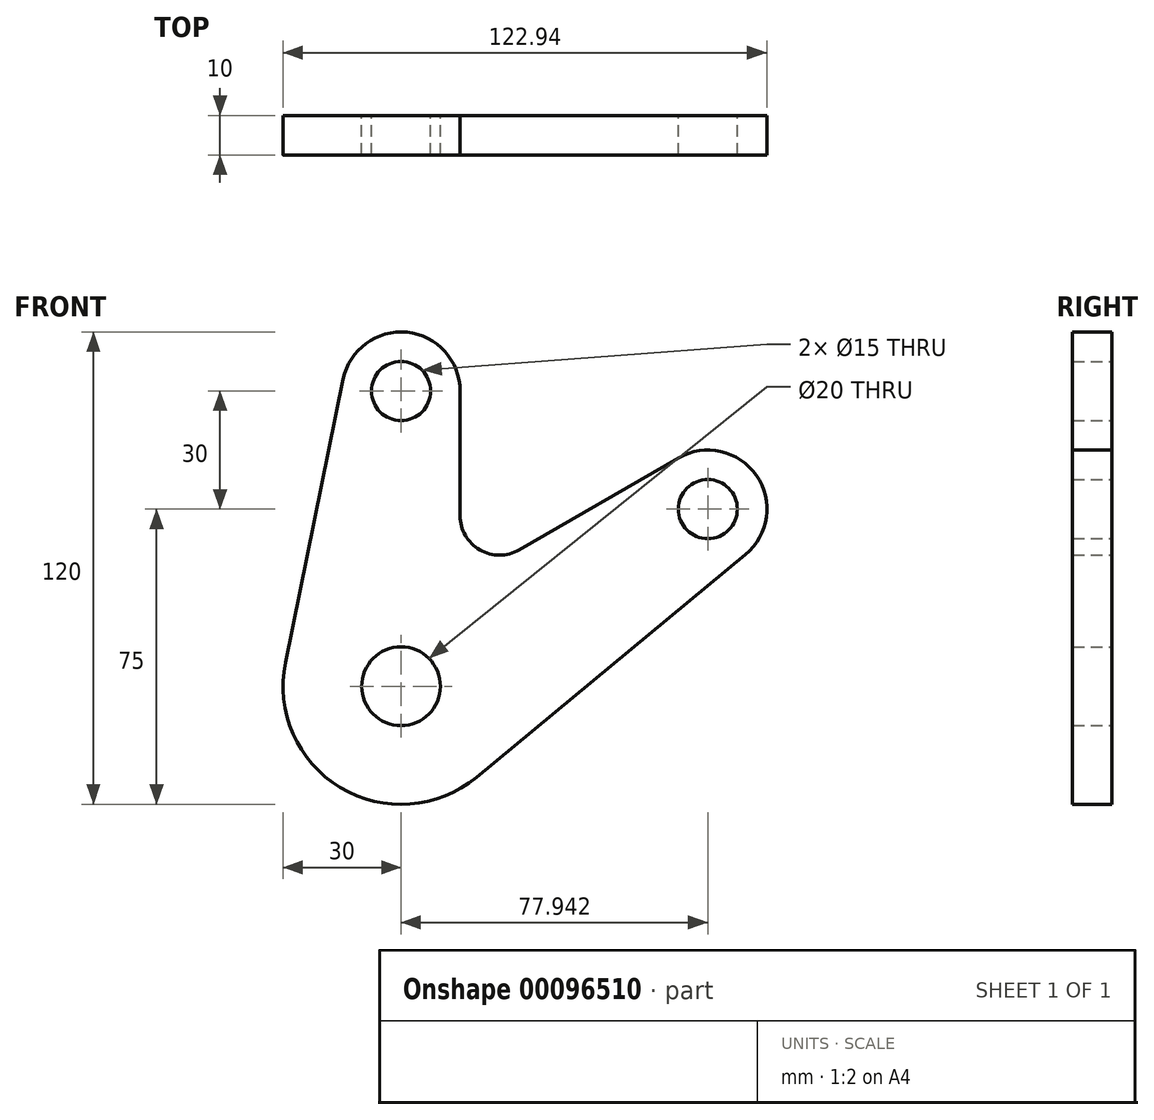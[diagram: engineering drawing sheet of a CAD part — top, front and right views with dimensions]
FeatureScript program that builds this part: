
annotation { "Feature Type Name" : "Feature", "Feature Type Description" : "" }
export const myFeature = defineFeature(function(context is Context, id is Id, definition is map)
    precondition{}
    {
        {
            var Q0;
            Q0=qCreatedBy(makeId("Front.planeOp"),FACE);
            var sketch = newSketch(context, id + "F0", { "sketchPlane" : qUnion([Q0])});
            skCircle(sketch, "E0", {"center": v(0, 0) * mm, "radius": 10 * mm});
            skCircle(sketch, "E1", {"center": v(0, 75) * mm, "radius": 7.5 * mm});
            skLineSegment(sketch, "E2", {"start": v(0, 0) * mm, "end": v(77.94, 45) * mm, "construction": true});
            skLineSegment(sketch, "E3", {"start": v(0, 0) * mm, "end": v(0, 75) * mm, "construction": true});
            skCircle(sketch, "E4", {"center": v(77.94, 45) * mm, "radius": 7.5 * mm});
            skArc(sketch, "E5", {"start": v(15, 75) * mm, "mid": v(1.5, 89.92) * mm, "end": v(-14.7, 78) * mm});
            skLineSegment(sketch, "E6", {"start": v(19.12, -23.12) * mm, "end": v(87.5, 33.44) * mm});
            skArc(sketch, "E7", {"start": v(87.5, 33.44) * mm, "mid": v(90.26, 53.56) * mm, "end": v(70.44, 58) * mm});
            skLineSegment(sketch, "E8", {"start": v(15, 25.98) * mm, "end": v(15, 25.98) * mm});
            skLineSegment(sketch, "E9", {"start": v(15, 43.3) * mm, "end": v(15, 75) * mm});
            skLineSegment(sketch, "E10", {"start": v(70.44, 58) * mm, "end": v(30, 34.64) * mm});
            skPoint(sketch, "E11.startSnap0", {"position": v(42.72, 41.99) * mm});
            skPoint(sketch, "E12.visualSharp", {"position": v(15, 25.98) * mm});
            skArc(sketch, "E12.filletArc", {"start": v(15, 43.3) * mm, "mid": v(20, 34.64) * mm, "end": v(30, 34.64) * mm});
            skLineSegment(sketch, "E13", {"start": v(-14.7, 78) * mm, "end": v(-29.4, 6) * mm});
            skArc(sketch, "E14", {"start": v(-29.4, 6) * mm, "mid": v(-15.44, -25.72) * mm, "end": v(19.12, -23.12) * mm});
            skSolve(sketch);
        }
        {
            var Q0;
            Q0 = qSketchRegion(id + "F0", true);
            extrude(context, id + "F1", {"entities" : qUnion([Q0]), "depth" : 10 * mm});
        }
    });
